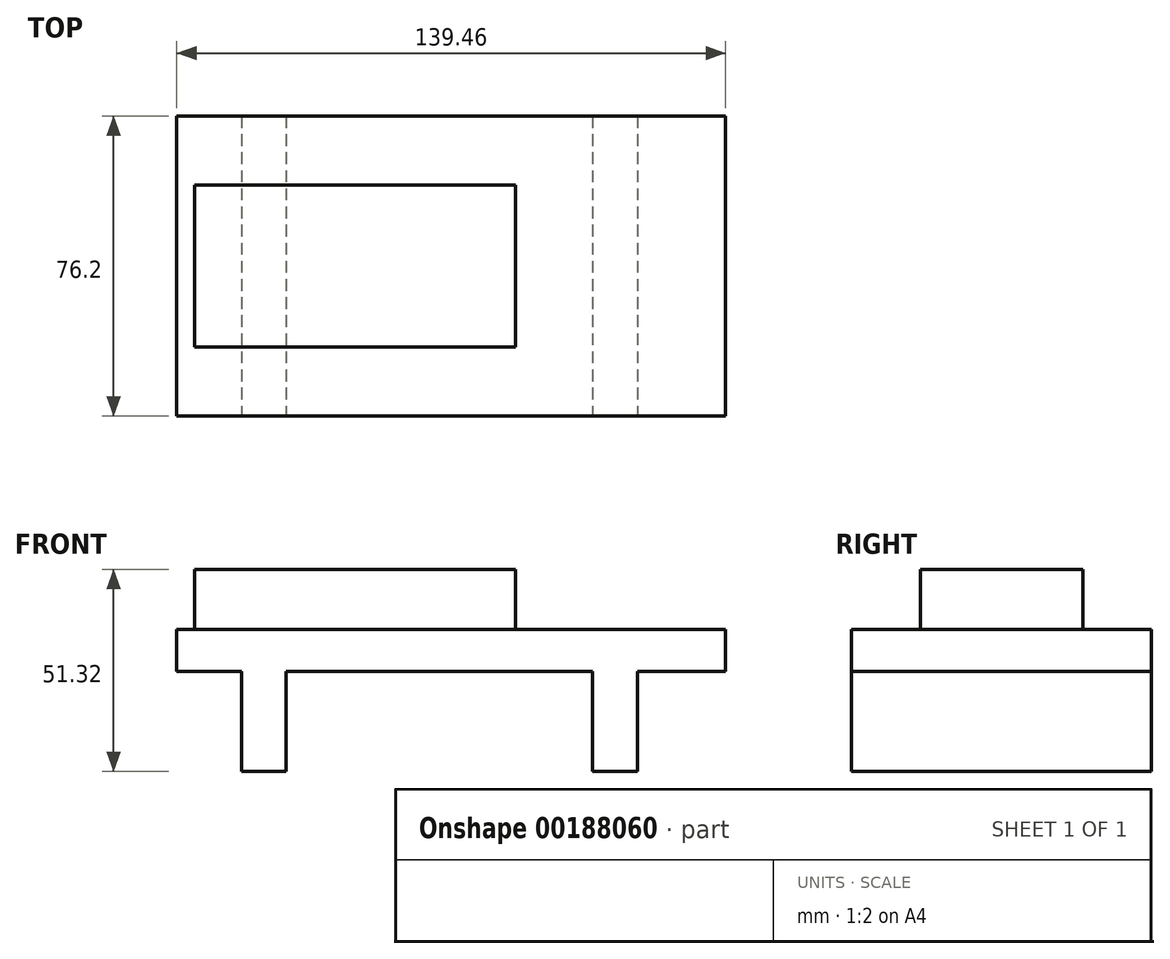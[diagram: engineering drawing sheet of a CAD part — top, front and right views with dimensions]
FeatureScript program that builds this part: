
annotation { "Feature Type Name" : "Feature", "Feature Type Description" : "" }
export const myFeature = defineFeature(function(context is Context, id is Id, definition is map)
    precondition{}
    {
        {
            var Q0;
            Q0=qCreatedBy(makeId("Front.planeOp"),FACE);
            var sketch = newSketch(context, id + "F0", { "sketchPlane" : qUnion([Q0])});
            skLineSegment(sketch, "E0.bottom", {"start": v(69.73, 5.34) * mm, "end": v(-69.73, 5.34) * mm});
            skLineSegment(sketch, "E0.top", {"start": v(69.73, -5.34) * mm, "end": v(-69.73, -5.34) * mm});
            skLineSegment(sketch, "E0.left", {"start": v(69.73, 5.34) * mm, "end": v(69.73, -5.34) * mm});
            skLineSegment(sketch, "E0.right", {"start": v(-69.73, 5.34) * mm, "end": v(-69.73, -5.34) * mm});
            skPoint(sketch, "E0.middle", {"position": v(0, 0) * mm});
            skSolve(sketch);
        }
        {
            var Q0;
            Q0=makeQuery(id+"F0.imprint","IMPRINT",FACE,{"disambiguationData":[TD([[makeQuery(id+"F0.imprint","IMPRINT",EDGE,{"derivedFrom":sQuery(id+"F0.wireOp",EDGE,"E0.bottom")}),1.0]])]});
            extrude(context, id + "F1", {"entities" : qUnion([Q0]), "depth" : 38.1 * mm});
        }
        {
            var Q0;
            Q0=makeQuery(id+"F1.opExtrude","CAP_FACE",FACE,{"disambiguationData":[OSD([sQuery(id+"F0.wireOp",EDGE,"E0.bottom"),sQuery(id+"F0.wireOp",EDGE,"E0.top"),sQuery(id+"F0.wireOp",EDGE,"E0.left"),sQuery(id+"F0.wireOp",EDGE,"E0.right")])],"isStart":true});
            var sketch = newSketch(context, id + "F2", { "sketchPlane" : qUnion([Q0])});
            skLineSegment(sketch, "E1.bottom", {"start": v(69.73, 5.34) * mm, "end": v(-69.73, 5.34) * mm});
            skLineSegment(sketch, "E1.top", {"start": v(69.73, -5.34) * mm, "end": v(-69.73, -5.34) * mm});
            skLineSegment(sketch, "E1.left", {"start": v(69.73, 5.34) * mm, "end": v(69.73, -5.34) * mm});
            skLineSegment(sketch, "E1.right", {"start": v(-69.73, 5.34) * mm, "end": v(-69.73, -5.34) * mm});
            skPoint(sketch, "E1.middle", {"position": v(0, 0) * mm});
            skSolve(sketch);
        }
        {
            var Q0;
            Q0=makeQuery(id+"F2.imprint","IMPRINT",FACE,{"disambiguationData":[TD([[makeQuery(id+"F2.imprint","IMPRINT",EDGE,{"derivedFrom":sQuery(id+"F2.wireOp",EDGE,"E1.bottom")}),-1.0]])]});
            extrude(context, id + "F3", {"entities" : qUnion([Q0]), "operationType" : NewBodyOperationType.ADD, "depth" : 38.1 * mm});
        }
        {
            var Q0;
            Q0=makeQuery(id+"F3.boolean.opBoolean","MERGE",FACE,{"derivedFrom":[makeQuery(id+"F1.opExtrude","SWEPT_FACE",FACE,{"disambiguationData":[OSD([sQuery(id+"F0.wireOp",EDGE,"E0.top")])]}),makeQuery(id+"F3.opExtrude","SWEPT_FACE",FACE,{"disambiguationData":[OSD([sQuery(id+"F2.wireOp",EDGE,"E1.top")])]})]});
            var sketch = newSketch(context, id + "F4", { "sketchPlane" : qUnion([Q0])});
            skLineSegment(sketch, "E2.bottom", {"start": v(43.45, -38.1) * mm, "end": v(54.78, -38.1) * mm});
            skLineSegment(sketch, "E2.top", {"start": v(43.45, 38.1) * mm, "end": v(54.78, 38.1) * mm});
            skLineSegment(sketch, "E2.left", {"start": v(43.45, -38.1) * mm, "end": v(43.45, 38.1) * mm});
            skLineSegment(sketch, "E2.right", {"start": v(54.78, -38.1) * mm, "end": v(54.78, 38.1) * mm});
            skPoint(sketch, "E2.middle", {"position": v(49.12, 0) * mm});
            skLineSegment(sketch, "E3.bottom", {"start": v(-41.93, -38.1) * mm, "end": v(-53.25, -38.1) * mm});
            skLineSegment(sketch, "E3.top", {"start": v(-41.93, 38.1) * mm, "end": v(-53.25, 38.1) * mm});
            skLineSegment(sketch, "E3.left", {"start": v(-41.93, -38.1) * mm, "end": v(-41.93, 38.1) * mm});
            skLineSegment(sketch, "E3.right", {"start": v(-53.25, -38.1) * mm, "end": v(-53.25, 38.1) * mm});
            skPoint(sketch, "E3.middle", {"position": v(-47.6, 0) * mm});
            skSolve(sketch);
        }
        {
            var Q0;
            Q0=makeQuery(id+"F4.imprint","IMPRINT",FACE,{"disambiguationData":[TD([[makeQuery(id+"F4.imprint","IMPRINT",EDGE,{"derivedFrom":sQuery(id+"F4.wireOp",EDGE,"E3.bottom")}),-1.0]])]});
            extrude(context, id + "F5", {"entities" : qUnion([Q0]), "operationType" : NewBodyOperationType.ADD, "depth" : 25.4 * mm});
        }
        {
            var Q0;
            {var subQ1=sQuery(id+"F2.wireOp",EDGE,"E1.top");var subQ2=sQuery(id+"F0.wireOp",EDGE,"E0.left");var subQ3=sQuery(id+"F0.wireOp",EDGE,"E0.top");Q0=makeQuery(id+"F5.boolean.opBoolean","SPLIT",FACE,{"disambiguationData":[TD([makeQuery(id+"F1.opExtrude","SWEPT_FACE",FACE,{"disambiguationData":[OSD([subQ2])]})])],"derivedFrom":makeQuery(id+"F3.boolean.opBoolean","MERGE",FACE,{"derivedFrom":[makeQuery(id+"F1.opExtrude","SWEPT_FACE",FACE,{"disambiguationData":[OSD([subQ3])]}),makeQuery(id+"F3.opExtrude","SWEPT_FACE",FACE,{"disambiguationData":[OSD([subQ1])]})]})});}
            var sketch = newSketch(context, id + "F6", { "sketchPlane" : qUnion([Q0])});
            skLineSegment(sketch, "E4.bottom", {"start": v(35.95, -38.1) * mm, "end": v(47.27, -38.1) * mm});
            skLineSegment(sketch, "E4.top", {"start": v(35.95, 38.1) * mm, "end": v(47.27, 38.1) * mm});
            skLineSegment(sketch, "E4.left", {"start": v(35.95, -38.1) * mm, "end": v(35.95, 38.1) * mm});
            skLineSegment(sketch, "E4.right", {"start": v(47.27, -38.1) * mm, "end": v(47.27, 38.1) * mm});
            skPoint(sketch, "E4.middle", {"position": v(41.6, 0) * mm});
            skSolve(sketch);
        }
        {
            var Q0;
            Q0=makeQuery(id+"F6.imprint","IMPRINT",FACE,{"disambiguationData":[TD([[makeQuery(id+"F6.imprint","IMPRINT",EDGE,{"derivedFrom":sQuery(id+"F6.wireOp",EDGE,"E4.bottom")}),-1.0]])]});
            extrude(context, id + "F7", {"entities" : qUnion([Q0]), "operationType" : NewBodyOperationType.ADD, "depth" : 25.4 * mm});
        }
        {
            var Q0;
            Q0=makeQuery(id+"F3.boolean.opBoolean","MERGE",FACE,{"derivedFrom":[makeQuery(id+"F1.opExtrude","SWEPT_FACE",FACE,{"disambiguationData":[OSD([sQuery(id+"F0.wireOp",EDGE,"E0.bottom")])]}),makeQuery(id+"F3.opExtrude","SWEPT_FACE",FACE,{"disambiguationData":[OSD([sQuery(id+"F2.wireOp",EDGE,"E1.bottom")])]})]});
            var sketch = newSketch(context, id + "F8", { "sketchPlane" : qUnion([Q0])});
            skLineSegment(sketch, "E5.bottom", {"start": v(16.29, -20.61) * mm, "end": v(-65.15, -20.61) * mm});
            skLineSegment(sketch, "E5.top", {"start": v(16.29, 20.61) * mm, "end": v(-65.15, 20.61) * mm});
            skLineSegment(sketch, "E5.left", {"start": v(16.29, -20.61) * mm, "end": v(16.29, 20.61) * mm});
            skLineSegment(sketch, "E5.right", {"start": v(-65.15, -20.61) * mm, "end": v(-65.15, 20.61) * mm});
            skPoint(sketch, "E5.middle", {"position": v(-24.43, 0) * mm});
            skSolve(sketch);
        }
        {
            var Q0;
            Q0=makeQuery(id+"F8.imprint","IMPRINT",FACE,{"disambiguationData":[TD([[makeQuery(id+"F8.imprint","IMPRINT",EDGE,{"derivedFrom":sQuery(id+"F8.wireOp",EDGE,"E5.bottom")}),-1.0]])]});
            extrude(context, id + "F9", {"entities" : qUnion([Q0]), "operationType" : NewBodyOperationType.ADD, "depth" : 15.24 * mm});
        }
        {
            var Q0;
            Q0=makeQuery(id+"F9.opExtrude","CAP_FACE",FACE,{"disambiguationData":[OSD([sQuery(id+"F8.wireOp",EDGE,"E5.bottom"),sQuery(id+"F8.wireOp",EDGE,"E5.top"),sQuery(id+"F8.wireOp",EDGE,"E5.left"),sQuery(id+"F8.wireOp",EDGE,"E5.right")])],"isStart":false});
            var sketch = newSketch(context, id + "F10", { "sketchPlane" : qUnion([Q0])});
            skCircle(sketch, "E6", {"center": v(-40.21, 0) * mm, "radius": 19.07 * mm});
            skSolve(sketch);
        }
        {
            var Q0;
            Q0=sQuery(id+"F10.wireOp",EDGE,"E6");
            extrude(context, id + "F11", {"bodyType" : ToolBodyType.SURFACE, "surfaceEntities" : qUnion([Q0]), "depth" : 12.7 * mm});
        }
    });
